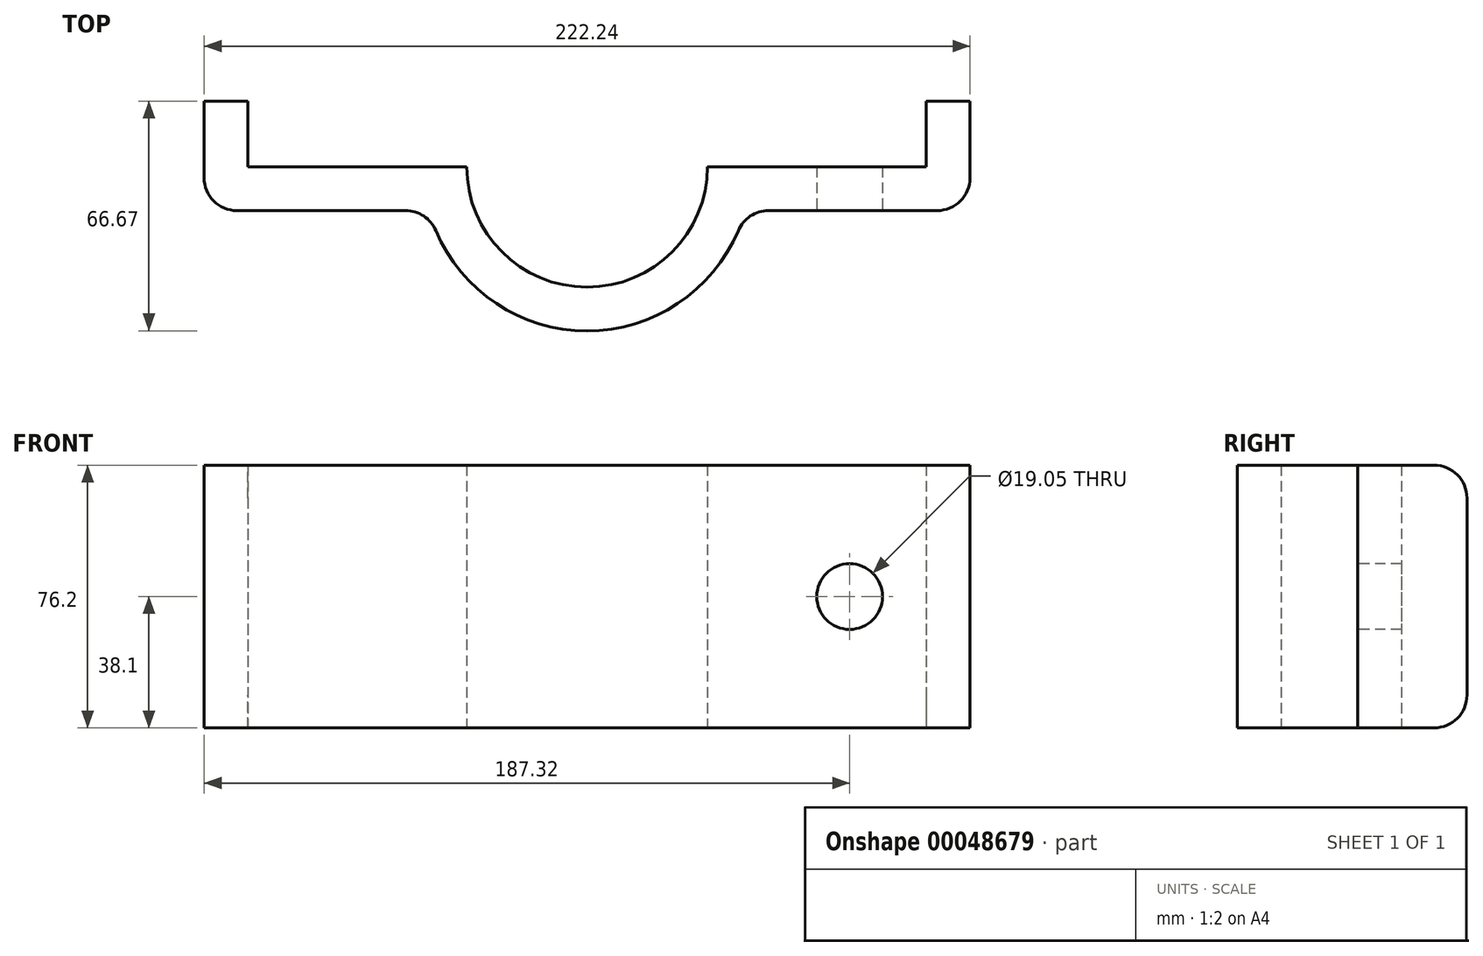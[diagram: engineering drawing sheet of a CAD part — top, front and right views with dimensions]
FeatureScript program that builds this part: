
annotation { "Feature Type Name" : "Feature", "Feature Type Description" : "" }
export const myFeature = defineFeature(function(context is Context, id is Id, definition is map)
    precondition{}
    {
        {
            var Q0;
            Q0=qCreatedBy(makeId("Top.planeOp"),FACE);
            var sketch = newSketch(context, id + "F0", { "sketchPlane" : qUnion([Q0])});
            skLineSegment(sketch, "E0.bottom", {"start": v(-111.13, 19.05) * mm, "end": v(-98.43, 19.05) * mm});
            skLineSegment(sketch, "E0.top", {"start": v(-111.13, -12.7) * mm, "end": v(-45.9, -12.7) * mm});
            skLineSegment(sketch, "E0.left", {"start": v(-111.13, 19.05) * mm, "end": v(-111.13, -12.7) * mm});
            skLineSegment(sketch, "E0.right", {"start": v(111.12, 19.05) * mm, "end": v(111.12, -12.7) * mm});
            skLineSegment(sketch, "E1", {"start": v(-98.42, 19.05) * mm, "end": v(-98.42, 0) * mm});
            skLineSegment(sketch, "E2", {"start": v(98.43, 0) * mm, "end": v(98.43, 19.05) * mm});
            skLineSegment(sketch, "E3.trimOffspring", {"start": v(98.43, 19.05) * mm, "end": v(111.13, 19.05) * mm});
            skArc(sketch, "E4", {"start": v(-34.93, 0) * mm, "mid": v(0, -34.93) * mm, "end": v(34.93, 0) * mm});
            skArc(sketch, "E5.0", {"start": v(-45.9, -12.7) * mm, "mid": v(0, -47.63) * mm, "end": v(45.9, -12.7) * mm});
            skLineSegment(sketch, "E6.trimOffspring", {"start": v(34.93, 0) * mm, "end": v(98.43, 0) * mm});
            skLineSegment(sketch, "E7.trimOffspring", {"start": v(45.9, -12.7) * mm, "end": v(111.13, -12.7) * mm});
            skLineSegment(sketch, "E8", {"start": v(-98.42, 0) * mm, "end": v(-34.93, 0) * mm});
            skSolve(sketch);
        }
        {
            var Q0;
            Q0=makeQuery(id+"F0.imprint","IMPRINT",FACE,{"disambiguationData":[TD([[makeQuery(id+"F0.imprint","IMPRINT",EDGE,{"derivedFrom":sQuery(id+"F0.wireOp",EDGE,"E0.bottom")}),-1.0]])]});
            extrude(context, id + "F1", {"entities" : qUnion([Q0]), "depth" : 76.2 * mm});
        }
        {
            var Q0;
            Q0=makeQuery(id+"F1.opExtrude","SWEPT_FACE",FACE,{"disambiguationData":[OSD([sQuery(id+"F0.wireOp",EDGE,"E7.trimOffspring")])]});
            var sketch = newSketch(context, id + "F2", { "sketchPlane" : qUnion([Q0])});
            skCircle(sketch, "E9", {"center": v(76.2, 38.1) * mm, "radius": 9.53 * mm});
            skCircle(sketch, "E10.MirrorC", {"center": v(-76.2, 38.1) * mm, "radius": 9.53 * mm});
            skSolve(sketch);
        }
        {
            var Q0;
            Q0=makeQuery(id+"F2.imprint","IMPRINT",FACE,{"disambiguationData":[TD([[makeQuery(id+"F2.imprint","IMPRINT",EDGE,{"derivedFrom":sQuery(id+"F2.wireOp",EDGE,"E10.MirrorC")}),-1.0]])]});
            var Q1;
            Q1=makeQuery(id+"F2.imprint","IMPRINT",FACE,{"disambiguationData":[TD([[makeQuery(id+"F2.imprint","IMPRINT",EDGE,{"derivedFrom":sQuery(id+"F2.wireOp",EDGE,"E9")}),1.0]])]});
            extrude(context, id + "F3", {"entities" : qUnion([Q0, Q1]), "operationType" : NewBodyOperationType.REMOVE, "endBound" : BoundingType.THROUGH_ALL, "oppositeDirection" : true, "depth" : 12.7 * mm});
        }
        {
            var Q0;
            Q0=makeQuery(id+"F1.opExtrude","SWEPT_EDGE",EDGE,{"disambiguationData":[OSD([sQuery(id+"F0.wireOp",EDGE,"E0.right"),sQuery(id+"F0.wireOp",EDGE,"E7.trimOffspring")])]});
            var Q1;
            Q1=makeQuery(id+"F1.opExtrude","SWEPT_EDGE",EDGE,{"disambiguationData":[OSD([sQuery(id+"F0.wireOp",EDGE,"E5.0"),sQuery(id+"F0.wireOp",EDGE,"E7.trimOffspring")])]});
            var Q2;
            Q2=makeQuery(id+"F1.opExtrude","SWEPT_EDGE",EDGE,{"disambiguationData":[OSD([sQuery(id+"F0.wireOp",EDGE,"E0.top"),sQuery(id+"F0.wireOp",EDGE,"E5.0")])]});
            var Q3;
            Q3=makeQuery(id+"F1.opExtrude","SWEPT_EDGE",EDGE,{"disambiguationData":[OSD([sQuery(id+"F0.wireOp",EDGE,"E0.top"),sQuery(id+"F0.wireOp",EDGE,"E0.left")])]});
            var Q4;
            Q4=makeQuery(id+"F1.opExtrude","CAP_EDGE",EDGE,{"disambiguationData":[OSD([sQuery(id+"F0.wireOp",EDGE,"E3.trimOffspring")])],"isStart":false});
            var Q5;
            Q5=makeQuery(id+"F1.opExtrude","CAP_EDGE",EDGE,{"disambiguationData":[OSD([sQuery(id+"F0.wireOp",EDGE,"E0.bottom")])],"isStart":false});
            var Q6;
            Q6=makeQuery(id+"F1.opExtrude","CAP_EDGE",EDGE,{"disambiguationData":[OSD([sQuery(id+"F0.wireOp",EDGE,"E3.trimOffspring")])],"isStart":true});
            var Q7;
            Q7=makeQuery(id+"F1.opExtrude","CAP_EDGE",EDGE,{"disambiguationData":[OSD([sQuery(id+"F0.wireOp",EDGE,"E0.bottom")])],"isStart":true});
            fillet(context, id + "F4", {"entities" : qUnion([Q0, Q1, Q2, Q3, Q4, Q5, Q6, Q7]), "radius" : 9.52 * mm, "allowEdgeOverflow" : false});
        }
    });
